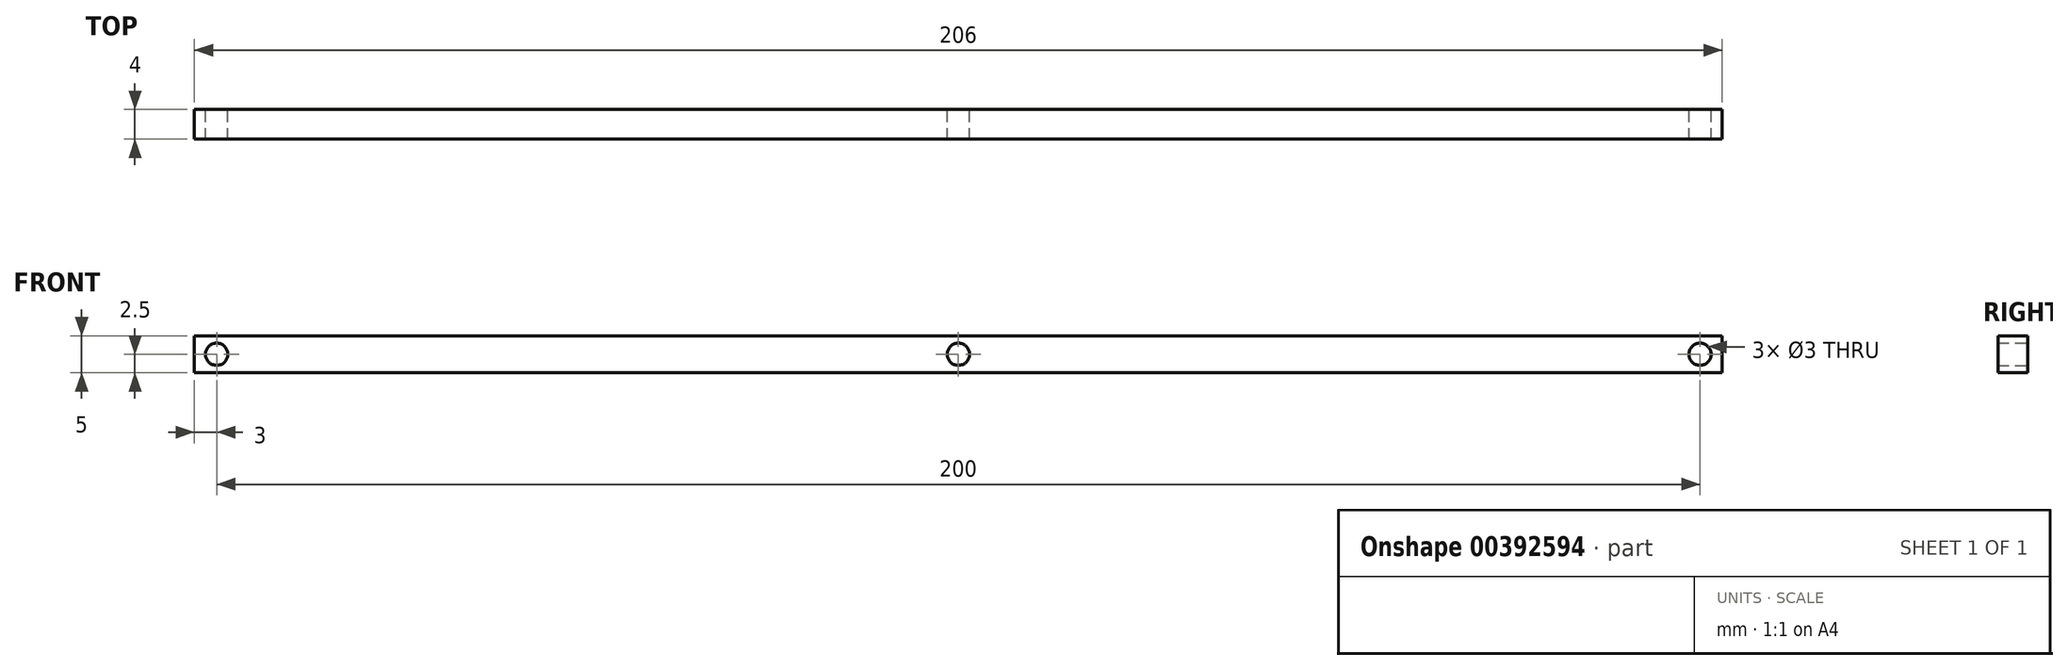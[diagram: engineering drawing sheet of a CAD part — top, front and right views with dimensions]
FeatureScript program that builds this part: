
annotation { "Feature Type Name" : "Feature", "Feature Type Description" : "" }
export const myFeature = defineFeature(function(context is Context, id is Id, definition is map)
    precondition{}
    {
        {
            var Q0;
            Q0=qCreatedBy(makeId("Front.planeOp"),FACE);
            var sketch = newSketch(context, id + "F0", { "sketchPlane" : qUnion([Q0])});
            skLineSegment(sketch, "E0.bottom", {"start": v(-143, 0) * mm, "end": v(63, 0) * mm});
            skLineSegment(sketch, "E0.top", {"start": v(-143, 5) * mm, "end": v(63, 5) * mm});
            skLineSegment(sketch, "E0.left", {"start": v(-143, 0) * mm, "end": v(-143, 5) * mm});
            skLineSegment(sketch, "E0.right", {"start": v(63, 0) * mm, "end": v(63, 5) * mm});
            skCircle(sketch, "E1", {"center": v(60, 2.5) * mm, "radius": 1.5 * mm});
            skCircle(sketch, "E2.1.0.0", {"center": v(-140, 2.5) * mm, "radius": 1.5 * mm});
            skLineSegment(sketch, "E2.direction1", {"start": v(60, 2.5) * mm, "end": v(-140, 2.5) * mm, "construction": true});
            skCircle(sketch, "E3", {"center": v(-40, 2.5) * mm, "radius": 1.5 * mm});
            skSolve(sketch);
        }
        {
            var Q0;
            Q0=makeQuery(id+"F0.imprint","IMPRINT",FACE,{"disambiguationData":[TD([[makeQuery(id+"F0.imprint","IMPRINT",EDGE,{"derivedFrom":sQuery(id+"F0.wireOp",EDGE,"E0.bottom")}),1.0]])]});
            var Q1;
            Q1=sQuery(id+"F0.wireOp",EDGE,"E0.top");
            extrude(context, id + "F1", {"entities" : qUnion([Q0]), "surfaceEntities" : qUnion([Q1]), "depth" : 4 * mm});
        }
    });
